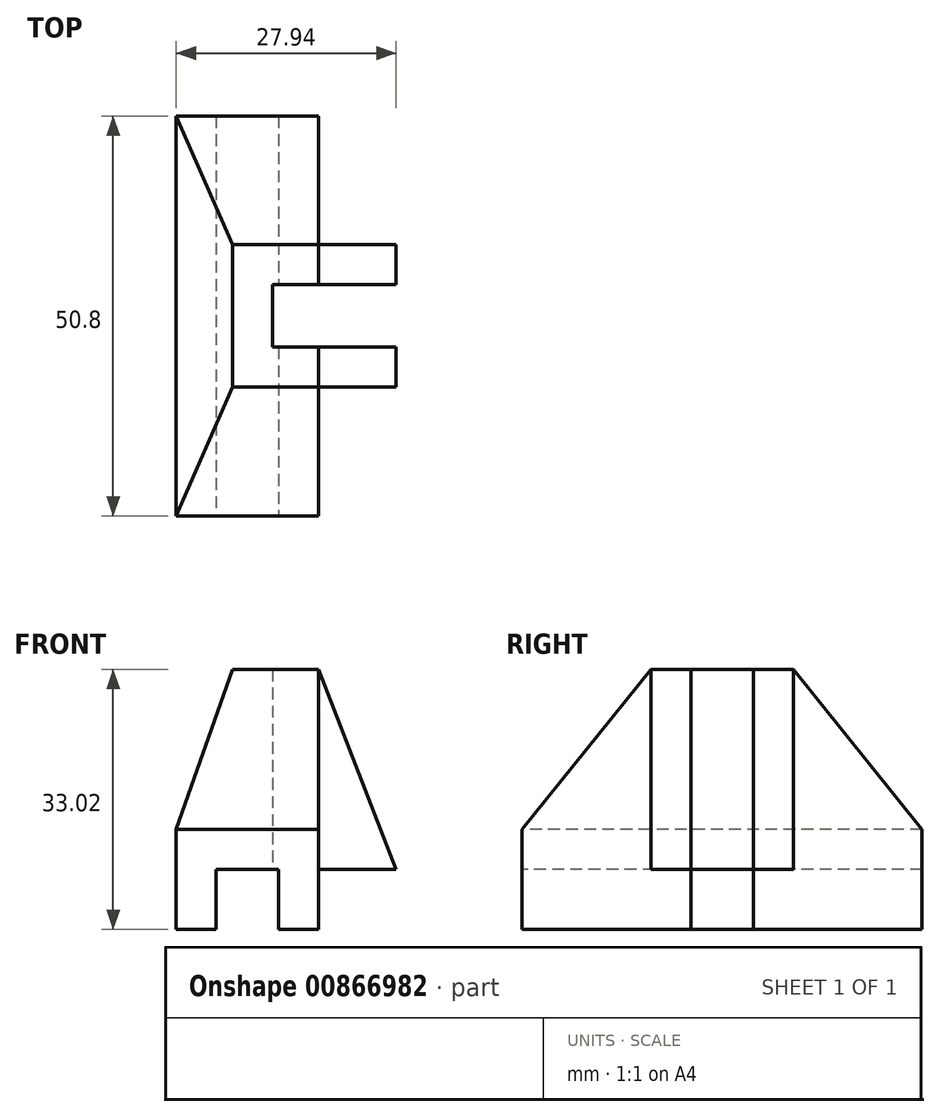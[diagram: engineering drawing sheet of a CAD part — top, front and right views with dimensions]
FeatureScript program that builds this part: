
annotation { "Feature Type Name" : "Feature", "Feature Type Description" : "" }
export const myFeature = defineFeature(function(context is Context, id is Id, definition is map)
    precondition{}
    {
        {
            var Q0;
            Q0=qCreatedBy(makeId("Top.planeOp"),FACE);
            var sketch = newSketch(context, id + "F0", { "sketchPlane" : qUnion([Q0])});
            skLineSegment(sketch, "E0.bottom", {"start": v(-13.97, -25.4) * mm, "end": v(13.97, -25.4) * mm});
            skLineSegment(sketch, "E0.top", {"start": v(-13.97, 25.4) * mm, "end": v(13.97, 25.4) * mm});
            skLineSegment(sketch, "E0.left", {"start": v(-13.97, -25.4) * mm, "end": v(-13.97, 25.4) * mm});
            skLineSegment(sketch, "E0.right", {"start": v(13.97, -25.4) * mm, "end": v(13.97, 25.4) * mm});
            skPoint(sketch, "E0.middle", {"position": v(0, 0) * mm});
            skSolve(sketch);
        }
        {
            var Q0;
            Q0 = qSketchRegion(id + "F0", true);
            extrude(context, id + "F1", {"entities" : qUnion([Q0]), "depth" : 33.02 * mm, "offsetDistance" : 25.4 * mm});
        }
        {
            var Q0;
            Q0=makeQuery(id+"F1.opExtrude","CAP_FACE",FACE,{"disambiguationData":[OSD([sQuery(id+"F0.wireOp",EDGE,"E0.bottom"),sQuery(id+"F0.wireOp",EDGE,"E0.top"),sQuery(id+"F0.wireOp",EDGE,"E0.left"),sQuery(id+"F0.wireOp",EDGE,"E0.right")])],"isStart":true});
            var sketch = newSketch(context, id + "F2", { "sketchPlane" : qUnion([Q0])});
            skPoint(sketch, "E1.middle", {"position": v(0, 0) * mm});
            skLineSegment(sketch, "E2.bottom", {"start": v(-8.9, -25.4) * mm, "end": v(-0.95, -25.4) * mm});
            skLineSegment(sketch, "E2.top", {"start": v(-8.9, 25.4) * mm, "end": v(-0.95, 25.4) * mm});
            skLineSegment(sketch, "E2.left", {"start": v(-8.9, -25.4) * mm, "end": v(-8.9, 25.4) * mm});
            skLineSegment(sketch, "E2.right", {"start": v(-0.95, -25.4) * mm, "end": v(-0.95, 25.4) * mm});
            skSolve(sketch);
        }
        {
            var Q0;
            Q0 = qSketchRegion(id + "F2", true);
            extrude(context, id + "F3", {"entities" : qUnion([Q0]), "operationType" : NewBodyOperationType.REMOVE, "oppositeDirection" : true, "depth" : 7.62 * mm, "offsetDistance" : 25.4 * mm});
        }
        {
            var Q0;
            {var subQ0=sQuery(id+"F0.wireOp",EDGE,"E0.bottom");var subQ1=sQuery(id+"F0.wireOp",EDGE,"E0.right");var subQ2=sQuery(id+"F0.wireOp",EDGE,"E0.top");Q0=makeQuery(id+"F3.boolean.opBoolean","SPLIT",FACE,{"disambiguationData":[TD([makeQuery(id+"F1.opExtrude","SWEPT_FACE",FACE,{"disambiguationData":[OSD([subQ1])]})])],"derivedFrom":makeQuery(id+"F1.opExtrude","CAP_FACE",FACE,{"disambiguationData":[OSD([subQ0,subQ2,sQuery(id+"F0.wireOp",EDGE,"E0.left"),subQ1])],"isStart":true})});}
            var sketch = newSketch(context, id + "F4", { "sketchPlane" : qUnion([Q0])});
            skLineSegment(sketch, "E3", {"start": v(0, 0) * mm, "end": v(13.97, 0) * mm, "construction": true});
            skLineSegment(sketch, "E4.bottom", {"start": v(-0.95, -3.97) * mm, "end": v(14.92, -3.97) * mm});
            skLineSegment(sketch, "E4.top", {"start": v(-0.95, 3.97) * mm, "end": v(14.92, 3.97) * mm});
            skLineSegment(sketch, "E4.left", {"start": v(-0.95, -3.97) * mm, "end": v(-0.95, 3.97) * mm});
            skLineSegment(sketch, "E4.right", {"start": v(14.92, -3.97) * mm, "end": v(14.92, 3.97) * mm});
            skPoint(sketch, "E4.middle", {"position": v(6.99, 0) * mm});
            skSolve(sketch);
        }
        {
            var Q0;
            Q0 = qSketchRegion(id + "F4", true);
            var Q1;
            Q1=makeQuery(id+"F3.boolean.opBoolean","COPY",FACE,{"derivedFrom":makeQuery(id+"F3.opExtrude","CAP_FACE",FACE,{"disambiguationData":[OSD([sQuery(id+"F2.wireOp",EDGE,"E2.bottom"),sQuery(id+"F2.wireOp",EDGE,"E2.top"),sQuery(id+"F2.wireOp",EDGE,"E2.left"),sQuery(id+"F2.wireOp",EDGE,"E2.right")])],"isStart":false})});
            extrude(context, id + "F5", {"entities" : qUnion([Q0]), "operationType" : NewBodyOperationType.REMOVE, "endBound" : BoundingType.UP_TO_SURFACE, "oppositeDirection" : true, "depth" : 25.4 * mm, "endBoundEntityFace" : qUnion([Q1]), "offsetDistance" : 25.4 * mm});
        }
        {
            var Q0;
            {var subQ0=sQuery(id+"F2.wireOp",EDGE,"E2.right");var subQ1=sQuery(id+"F2.wireOp",EDGE,"E2.left");var subQ2=sQuery(id+"F2.wireOp",EDGE,"E2.top");var subQ3=sQuery(id+"F2.wireOp",EDGE,"E2.bottom");Q0=makeQuery(id+"F5.boolean.opBoolean","MERGE",FACE,{"derivedFrom":[makeQuery(id+"F3.boolean.opBoolean","COPY",FACE,{"derivedFrom":makeQuery(id+"F3.opExtrude","CAP_FACE",FACE,{"disambiguationData":[OSD([subQ3,subQ2,subQ1,subQ0])],"isStart":false})}),makeQuery(id+"F5.opExtrude","CAP_FACE",FACE,{"disambiguationData":[OSD([subQ3,subQ2,subQ1,subQ0])],"isStart":false})]});}
            var sketch = newSketch(context, id + "F6", { "sketchPlane" : qUnion([Q0])});
            skLineSegment(sketch, "E5.0", {"start": v(13.97, -3.97) * mm, "end": v(13.97, 3.97) * mm});
            skLineSegment(sketch, "E6", {"start": v(13.97, 3.97) * mm, "end": v(-1.71, 3.97) * mm});
            skLineSegment(sketch, "E7", {"start": v(-1.71, 3.97) * mm, "end": v(-1.71, -3.97) * mm});
            skLineSegment(sketch, "E8", {"start": v(-1.71, -3.97) * mm, "end": v(13.97, -3.97) * mm});
            skSolve(sketch);
        }
        {
            var Q0;
            Q0 = qSketchRegion(id + "F6", true);
            extrude(context, id + "F7", {"entities" : qUnion([Q0]), "operationType" : NewBodyOperationType.REMOVE, "endBound" : BoundingType.UP_TO_NEXT, "oppositeDirection" : true, "depth" : 25.4 * mm, "offsetDistance" : 25.4 * mm});
        }
        {
            var Q0;
            {var subQ0=sQuery(id+"F0.wireOp",EDGE,"E0.top");var subQ1=makeQuery(id+"F1.opExtrude","SWEPT_FACE",FACE,{"disambiguationData":[OSD([subQ0])]});var subQ2=sQuery(id+"F0.wireOp",EDGE,"E0.right");var subQ3=makeQuery(id+"F1.opExtrude","SWEPT_FACE",FACE,{"disambiguationData":[OSD([subQ2])]});var subQ5=sQuery(id+"F0.wireOp",EDGE,"E0.bottom");Q0=makeQuery(id+"F5.boolean.opBoolean","SPLIT",FACE,{"disambiguationData":[TD([subQ1])],"derivedFrom":makeQuery(id+"F3.boolean.opBoolean","SPLIT",FACE,{"disambiguationData":[TD([subQ3])],"derivedFrom":makeQuery(id+"F1.opExtrude","CAP_FACE",FACE,{"disambiguationData":[OSD([subQ5,subQ0,sQuery(id+"F0.wireOp",EDGE,"E0.left"),subQ2])],"isStart":true})})});}
            var sketch = newSketch(context, id + "F8", { "sketchPlane" : qUnion([Q0])});
            skLineSegment(sketch, "E9.bottom", {"start": v(13.97, -25.4) * mm, "end": v(4.13, -25.4) * mm});
            skLineSegment(sketch, "E9.top", {"start": v(13.97, -9.05) * mm, "end": v(4.13, -9.05) * mm});
            skLineSegment(sketch, "E9.left", {"start": v(13.97, -25.4) * mm, "end": v(13.97, -9.05) * mm});
            skLineSegment(sketch, "E9.right", {"start": v(4.13, -25.4) * mm, "end": v(4.13, -9.05) * mm});
            skLineSegment(sketch, "E10.MirrorCS", {"start": v(13.97, 9.05) * mm, "end": v(4.13, 9.05) * mm});
            skLineSegment(sketch, "E11.MirrorCS", {"start": v(4.13, 25.4) * mm, "end": v(4.13, 9.05) * mm});
            skLineSegment(sketch, "E12.MirrorCS", {"start": v(13.97, 25.4) * mm, "end": v(4.13, 25.4) * mm});
            skLineSegment(sketch, "E13.MirrorCS", {"start": v(13.97, 25.4) * mm, "end": v(13.97, 9.05) * mm});
            skSolve(sketch);
        }
        {
            var Q0;
            Q0 = qSketchRegion(id + "F8", true);
            extrude(context, id + "F9", {"entities" : qUnion([Q0]), "operationType" : NewBodyOperationType.REMOVE, "endBound" : BoundingType.UP_TO_NEXT, "oppositeDirection" : true, "depth" : 25.4 * mm, "offsetDistance" : 25.4 * mm});
        }
        {
            var Q0;
            Q0=makeQuery(id+"F1.opExtrude","SWEPT_FACE",FACE,{"disambiguationData":[OSD([sQuery(id+"F0.wireOp",EDGE,"E0.left")])]});
            var sketch = newSketch(context, id + "F10", { "sketchPlane" : qUnion([Q0])});
            skLineSegment(sketch, "E14.0", {"start": v(-3.97, 33.02) * mm, "end": v(-3.97, 0) * mm, "construction": true});
            skLineSegment(sketch, "E15.0", {"start": v(3.97, 33.02) * mm, "end": v(3.97, 0) * mm, "construction": true});
            skLineSegment(sketch, "E16", {"start": v(-3.97, 33.02) * mm, "end": v(-9.05, 33.02) * mm, "construction": true});
            skLineSegment(sketch, "E17", {"start": v(-9.05, 33.02) * mm, "end": v(-25.4, 12.7) * mm});
            skLineSegment(sketch, "E18", {"start": v(-25.4, 12.7) * mm, "end": v(-25.4, 0) * mm, "construction": true});
            skLineSegment(sketch, "E19", {"start": v(-25.4, 12.7) * mm, "end": v(-25.4, 33.02) * mm});
            skLineSegment(sketch, "E20", {"start": v(-25.4, 33.02) * mm, "end": v(-9.05, 33.02) * mm});
            skLineSegment(sketch, "E21.MirrorCS", {"start": v(9.05, 33.02) * mm, "end": v(25.4, 12.7) * mm});
            skLineSegment(sketch, "E22.MirrorCS", {"start": v(25.4, 33.02) * mm, "end": v(9.05, 33.02) * mm});
            skLineSegment(sketch, "E23.MirrorCS", {"start": v(25.4, 12.7) * mm, "end": v(25.4, 33.02) * mm});
            skSolve(sketch);
        }
        {
            var Q0;
            Q0 = qSketchRegion(id + "F10", true);
            extrude(context, id + "F11", {"entities" : qUnion([Q0]), "operationType" : NewBodyOperationType.REMOVE, "endBound" : BoundingType.THROUGH_ALL, "oppositeDirection" : true, "depth" : 25.4 * mm, "offsetDistance" : 25.4 * mm});
        }
        {
            var Q0;
            Q0=qCreatedBy(makeId("Front.planeOp"),FACE);
            var sketch = newSketch(context, id + "F12", { "sketchPlane" : qUnion([Q0])});
            skLineSegment(sketch, "E24.0", {"start": v(-1.71, 33.02) * mm, "end": v(-1.71, 7.62) * mm, "construction": true});
            skLineSegment(sketch, "E25.0", {"start": v(-13.97, 33.02) * mm, "end": v(-13.97, 12.7) * mm});
            skLineSegment(sketch, "E26", {"start": v(-13.97, 33.02) * mm, "end": v(-6.8, 33.02) * mm});
            skLineSegment(sketch, "E27", {"start": v(-6.8, 33.02) * mm, "end": v(-13.97, 12.7) * mm});
            skSolve(sketch);
        }
        {
            var Q0;
            Q0 = qSketchRegion(id + "F12", true);
            extrude(context, id + "F13", {"entities" : qUnion([Q0]), "operationType" : NewBodyOperationType.REMOVE, "endBound" : BoundingType.THROUGH_ALL, "oppositeDirection" : true, "depth" : 25.4 * mm, "offsetDistance" : 25.4 * mm, "hasSecondDirection" : true, "secondDirectionOppositeDirection" : false, "secondDirectionDepth" : 25.4 * mm});
        }
        {
            var Q0;
            Q0=makeQuery(id+"F9.boolean.opBoolean","COPY",FACE,{"derivedFrom":makeQuery(id+"F9.opExtrude","SWEPT_FACE",FACE,{"disambiguationData":[OSD([sQuery(id+"F8.wireOp",EDGE,"E9.top")])]})});
            var sketch = newSketch(context, id + "F14", { "sketchPlane" : qUnion([Q0])});
            skLineSegment(sketch, "E28.0", {"start": v(-13.97, 0) * mm, "end": v(-4.13, 0) * mm});
            skLineSegment(sketch, "E29.0", {"start": v(-13.97, 33.02) * mm, "end": v(-13.97, 0) * mm});
            skLineSegment(sketch, "E30", {"start": v(-4.13, 7.62) * mm, "end": v(-13.97, 7.62) * mm});
            skLineSegment(sketch, "E31", {"start": v(-4.13, 0) * mm, "end": v(-4.13, 7.62) * mm});
            skSolve(sketch);
        }
        {
            var Q0;
            Q0 = qSketchRegion(id + "F14", true);
            extrude(context, id + "F15", {"entities" : qUnion([Q0]), "operationType" : NewBodyOperationType.REMOVE, "endBound" : BoundingType.THROUGH_ALL, "oppositeDirection" : true, "depth" : 25.4 * mm, "offsetDistance" : 25.4 * mm});
        }
        {
            var Q0;
            Q0=makeQuery(id+"F9.boolean.opBoolean","COPY",FACE,{"derivedFrom":makeQuery(id+"F9.opExtrude","SWEPT_FACE",FACE,{"disambiguationData":[OSD([sQuery(id+"F8.wireOp",EDGE,"E10.MirrorCS")])]})});
            var sketch = newSketch(context, id + "F16", { "sketchPlane" : qUnion([Q0])});
            skLineSegment(sketch, "E32", {"start": v(4.13, 33.02) * mm, "end": v(13.97, 7.62) * mm});
            skLineSegment(sketch, "E33", {"start": v(4.13, 33.02) * mm, "end": v(13.97, 33.02) * mm});
            skLineSegment(sketch, "E34", {"start": v(13.97, 33.02) * mm, "end": v(13.97, 7.62) * mm});
            skSolve(sketch);
        }
        {
            var Q0;
            Q0 = qSketchRegion(id + "F16", true);
            extrude(context, id + "F17", {"entities" : qUnion([Q0]), "operationType" : NewBodyOperationType.REMOVE, "endBound" : BoundingType.THROUGH_ALL, "oppositeDirection" : true, "depth" : 25.4 * mm, "offsetDistance" : 25.4 * mm});
        }
    });
